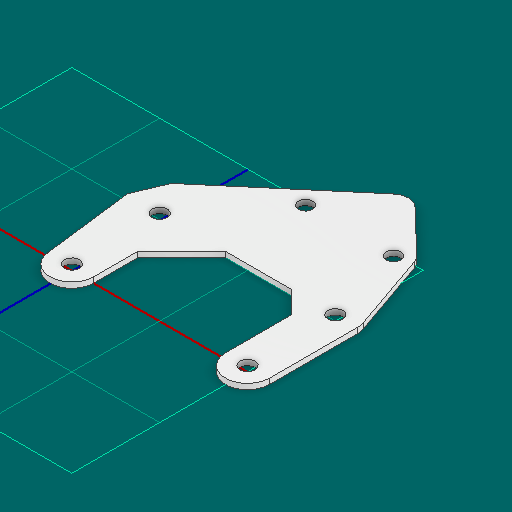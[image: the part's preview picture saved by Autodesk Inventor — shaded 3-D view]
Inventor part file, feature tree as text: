
AUTODESK INVENTOR PART (.ipt)
format: ipt  version: 2025 (Build 290162000, 162)  size: 159,232 bytes
history: native  units: in
note: dims shown in document units (in); Inventor stores cm internally (conversion verified against a paired STEP export)
features: other x6, sketch x1
ambient origin geometry x8: Origin, YZ Plane, XZ Plane, XY Plane, X Axis, Y Axis, Z Axis, Center Point
bodies: Solid1 (feature_tree)
feature tree (7):
  other  "gusset.ipt"
  other  "Blocks"
  other  "main"
  other  "Solid1::gusset.ipt"
  other  "TaggingFeature1"
  sketch  "Sketch1"  dims[d0=0.3937in d1=0.375in d2=0.5in d3=0.5in d4=0.25in d5=0.25in d6=0.164in d7=0.1875in d9=0.125in d12=1.911in d14=0.125in d16=1.0in d18=0.25in d17=1.9106in]
  other  "main:1"
